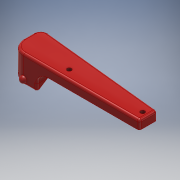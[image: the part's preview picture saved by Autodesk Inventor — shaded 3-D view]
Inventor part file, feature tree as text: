
AUTODESK INVENTOR PART (.ipt)
format: ipt  version: 2018.3 (Build 223284000, 284)  size: 246,784 bytes
history: native  units: mm
features: fillet x6, extrude x4, sketch x4, plane x1, chamfer x1, revolve x1
ambient origin geometry x8: Origin, YZ Plane, XZ Plane, XY Plane, X Axis, Y Axis, Z Axis, Center Point
bodies: Solid1 (feature_tree)
feature tree (17):
  extrude  "Extrusion1"  Depth=14.0mm
  extrude  "Extrusion2"  Depth=2.0mm
  extrude  "Extrusion3"  Depth=33.0mm
  plane  "Work Plane1"
  fillet  "Fillet1"  Radius=3.0mm
  chamfer  "Chamfer1"  Distance=12.0mm
  revolve  "Revolution2"  [1 undecoded]
  fillet  "Fillet6"  Radius=4.0mm
  fillet  "Fillet7"  Radius=6.0mm
  fillet  "Fillet8"  Radius=3.0mm
  fillet  "Fillet9"  Radius=3.0mm
  extrude  "Extrusion4"  TaperAngle=180.0deg  [1 undecoded]
  fillet  "Fillet10"  Radius=3.0mm
  sketch  "Sketch1"  dims[d0=58.0mm d1=14.0mm]
  sketch  "Sketch2"  dims[d2=4.0mm d3=0.0mm d4=2.0mm]
  sketch  "Sketch3"  dims[d6=2.0mm d7=33.0mm d8=3.0mm d9=0.0mm]
  sketch  "Sketch6"  dims[d10=9.0mm d11=12.0mm d12=0.0mm d17=6.0mm d22=4.0mm d23=6.0mm d24=58.0mm d25=45.0deg d26=3.0mm d27=3.0mm d28=180.0deg d29=3.0mm d30=1.0mm d31=1.0mm d32=1.0mm d33=4.0mm d34=1.0mm d35=0.0mm d36=5.0mm]
note: 2 required parameter values undecoded (feature->parameter linkage not recoverable at this tier; creation-order binding heuristic only, values carry confidence <= 0.55)